# Revit family: Fixture_Support-Water_Closet-Zurn-Carrier-Vertical-Z1204-ND
name_source: partatom
category: Plumbing Fixtures
units: mm (PartAtom-declared; Revit-internal decimal feet)

## family parameters
Always vertical = Yes
Cut with Voids When Loaded = No
Maintain Annotation Orientation = No
OmniClass Number = 23.45.55.11
OmniClass Title = Sanitary Components
Part Type = Normal
Room Calculation Point = No
Round Connector Dimension = Use Radius
Shared = No
Work Plane-Based = No

## types (1)
- Z1204-ND4 - 4 Inch Outlet
    Approx . Weight = 139.00 lb
    Assembly Code = D2030100
    CW Connection = No
    CWFU = 0
    Coupling = Steel-Zurn-Metal
    Default Elevation = 25 "
    Description = ADJUSTABLE VERTICAL SIPHON JET NO-HUB
    Diameter of Coupling = 4.625 "
    Dimension (E) = 6.625 "
    Dimension (N) = 13.25 "
    Dimesion (D) = 5 "
    Dimesion (H) = 7.688 "
    HW Connection = No
    HWFU = 0
    Inlet/Outlet Radius = 2 "
    Main Material = Iron - Zurn - Cast - Painted - Blue
    Manufacturer = Zurn Water, LLC
    Manufacurer Brand = Zurn
    Model = Z1204-ND
    Modified Date = 10/17/2025
    Outlet Radius Actual (A) = 2.25 "
    Outlet Radius Nominal (A) = 2 "
    Product Documentation Link = https://files.zurn.com
    Product Installation Sheet URL = https://files.zurn.com
    Product Page URL = https://www.zurn.com
    Product data url = https://www.bimobject.com
    Total length of connector = 14 "
    URL = www.zurn.com
    Vent Connection = Yes
    Vent Radius = 1 "
    WFU = 1
    Waste Connection = Yes
    Water Closet Inlet Radius = 1.5 "

## geometry (parser evidence)
native form markers: Sweep x16
no freeform markers — native parametric forms only
